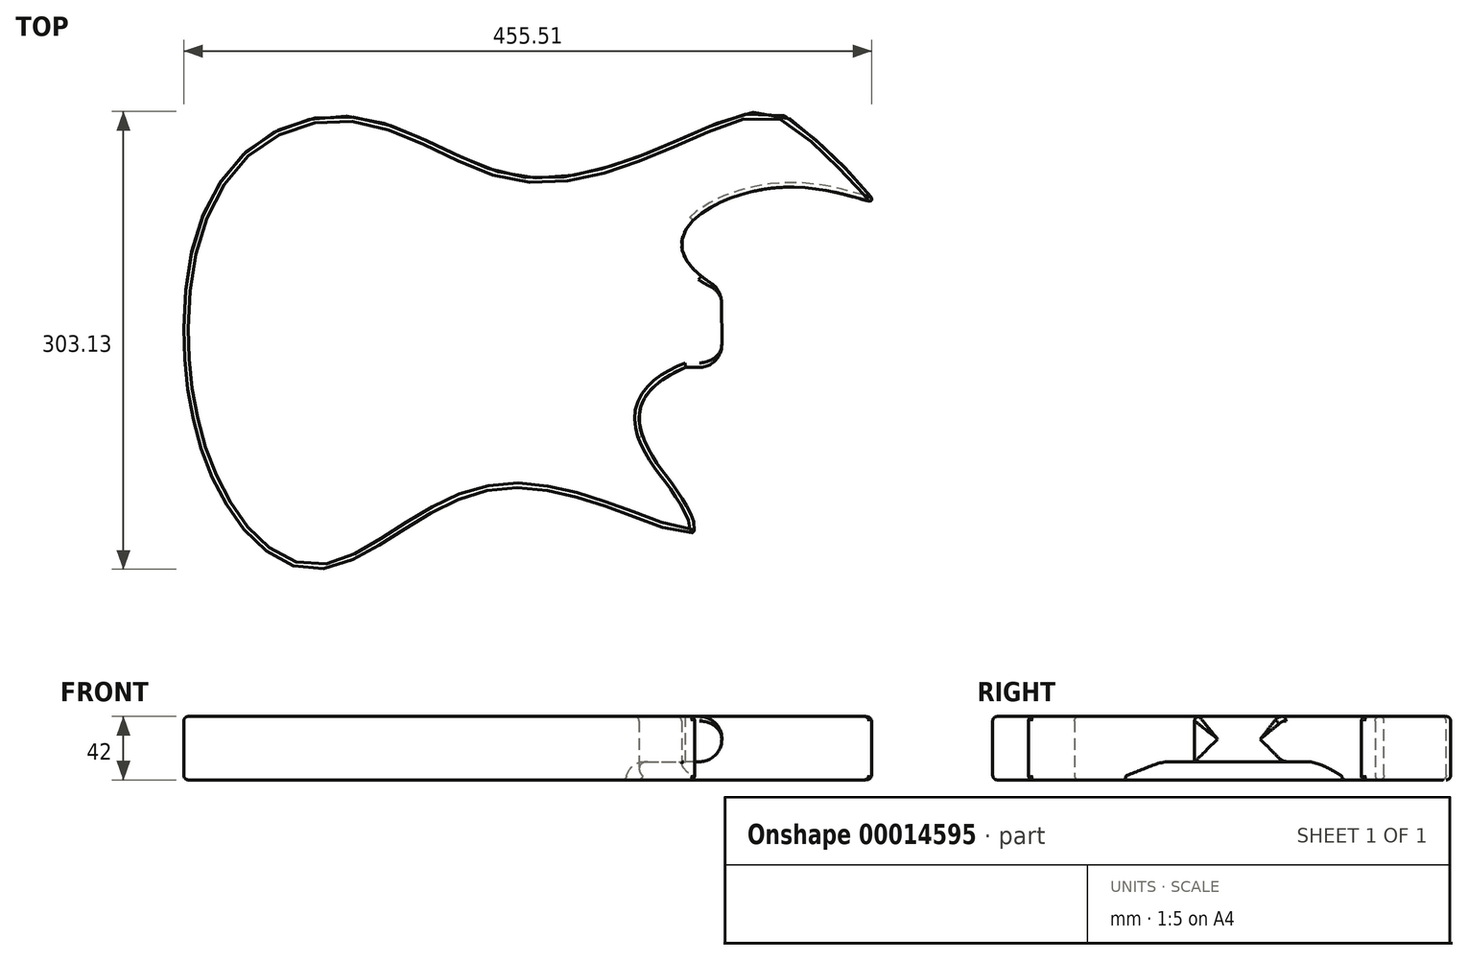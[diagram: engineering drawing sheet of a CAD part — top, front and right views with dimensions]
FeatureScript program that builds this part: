
annotation { "Feature Type Name" : "Feature", "Feature Type Description" : "" }
export const myFeature = defineFeature(function(context is Context, id is Id, definition is map)
    precondition{}
    {
        {
            var Q0;
            Q0=qCreatedBy(makeId("Top.planeOp"),FACE);
            var sketch = newSketch(context, id + "F0", { "sketchPlane" : qUnion([Q0])});
            skLineSegment(sketch, "E0", {"start": v(0, 450.63) * mm, "end": v(0, -420.06) * mm, "construction": true});
            skLineSegment(sketch, "E1", {"start": v(-1025.75, 0) * mm, "end": v(982.4, 0) * mm, "construction": true});
            skLineSegment(sketch, "E2", {"start": v(647.37, 21.5) * mm, "end": v(0, 27.92) * mm, "construction": true});
            skLineSegment(sketch, "E3.0.MirrorCS", {"start": v(647.37, -21.5) * mm, "end": v(0, -27.92) * mm, "construction": true});
            skLineSegment(sketch, "E4.0.MirrorCS", {"start": v(964.42, -135) * mm, "end": v(-680.01, -135) * mm, "construction": true});
            skPoint(sketch, "E5", {"position": v(192.37, -26) * mm});
            skPoint(sketch, "E6", {"position": v(215.87, 25.78) * mm});
            skFitSpline(sketch, "E7", {"points": [v(-139.95, 0) * mm, v(-52.8, -159.6) * mm, v(73.18, -105.7) * mm, v(197.21, -135) * mm, v(184.87, -105.05) * mm, v(169.29, -82.97) * mm, v(192.37, -26) * mm], "startDerivative": vector(-8.4, -1150.65) * mm, "endDerivative": vector(902.54, 365.45) * mm});
            skFitSpline(sketch, "E8", {"points": [v(215.87, 25.78) * mm, v(246.74, 92.46) * mm, v(315.54, 85.04) * mm, v(281.76, 121.56) * mm, v(245.96, 143.5) * mm, v(174.14, 118.99) * mm, v(75.44, 101.73) * mm, v(-31.82, 140.35) * mm, v(-139.95, 0) * mm], "startDerivative": vector(-1467.14, 819.4) * mm, "endDerivative": vector(0, -1755.16) * mm});
            skLineSegment(sketch, "E9", {"start": v(215.87, 25.78) * mm, "end": v(216.38, -25.77) * mm});
            skLineSegment(sketch, "E10", {"start": v(216.38, -25.77) * mm, "end": v(192.37, -26) * mm});
            skSolve(sketch);
        }
        {
            var Q0;
            Q0=makeQuery(id+"F0.imprint","IMPRINT",FACE,{"disambiguationData":[TD([[makeQuery(id+"F0.imprint","IMPRINT",EDGE,{"derivedFrom":sQuery(id+"F0.wireOp",EDGE,"E7")}),1.0]])]});
            extrude(context, id + "F1", {"entities" : qUnion([Q0]), "oppositeDirection" : true, "depth" : 42 * mm});
        }
        {
            var Q0;
            Q0=makeQuery(id+"F1.opExtrude","CAP_FACE",FACE,{"disambiguationData":[OSD([sQuery(id+"F0.wireOp",EDGE,"E7"),sQuery(id+"F0.wireOp",EDGE,"E8"),sQuery(id+"F0.wireOp",EDGE,"E9"),sQuery(id+"F0.wireOp",EDGE,"E10")])],"isStart":false});
            var sketch = newSketch(context, id + "F2", { "sketchPlane" : qUnion([Q0])});
            skArc(sketch, "E11", {"start": v(167.67, 80.11) * mm, "mid": v(155.83, -4.5) * mm, "end": v(202.55, -76.02) * mm});
            skLineSegment(sketch, "E12", {"start": v(202.55, -76.02) * mm, "end": v(243.56, 30.37) * mm});
            skLineSegment(sketch, "E13", {"start": v(243.56, 30.37) * mm, "end": v(167.67, 80.11) * mm});
            skSolve(sketch);
        }
        {
            var Q0;
            Q0 = qSketchRegion(id + "F2", true);
            extrude(context, id + "F3", {"entities" : qUnion([Q0]), "operationType" : NewBodyOperationType.REMOVE, "oppositeDirection" : true, "depth" : 12 * mm});
        }
        {
            var Q0;
            Q0=makeQuery(id+"F3.boolean.opBoolean","COPY",EDGE,{"derivedFrom":makeQuery(id+"F3.opExtrude","CAP_EDGE",EDGE,{"disambiguationData":[OSD([sQuery(id+"F2.wireOp",EDGE,"E11")])],"isStart":false})});
            fillet(context, id + "F4", {"entities" : qUnion([Q0]), "radius" : 12 * mm, "allowEdgeOverflow" : false});
        }
        {
            var Q0;
            Q0=makeQuery(id+"F1.opExtrude","CAP_FACE",FACE,{"disambiguationData":[OSD([sQuery(id+"F0.wireOp",EDGE,"E7"),sQuery(id+"F0.wireOp",EDGE,"E8"),sQuery(id+"F0.wireOp",EDGE,"E9"),sQuery(id+"F0.wireOp",EDGE,"E10")])],"isStart":false});
            fillet(context, id + "F5", {"entities" : qUnion([Q0]), "radius" : 3 * mm, "tangentPropagation" : true, "allowEdgeOverflow" : false});
        }
        {
            var Q0;
            Q0=makeQuery(id+"F1.opExtrude","CAP_EDGE",EDGE,{"disambiguationData":[OSD([sQuery(id+"F0.wireOp",EDGE,"E8")])],"isStart":true});
            var Q1;
            Q1=makeQuery(id+"F1.opExtrude","CAP_EDGE",EDGE,{"disambiguationData":[OSD([sQuery(id+"F0.wireOp",EDGE,"E7")])],"isStart":true});
            var Q2;
            Q2=makeQuery(id+"F1.opExtrude","CAP_EDGE",EDGE,{"disambiguationData":[OSD([sQuery(id+"F0.wireOp",EDGE,"E10")])],"isStart":true});
            fillet(context, id + "F6", {"entities" : qUnion([Q0, Q1, Q2]), "radius" : 3 * mm, "tangentPropagation" : true, "allowEdgeOverflow" : false});
        }
        {
            var Q0;
            Q0=makeQuery(id+"F1.opExtrude","SWEPT_FACE",FACE,{"disambiguationData":[OSD([sQuery(id+"F0.wireOp",EDGE,"E9")])]});
            fillet(context, id + "F7", {"entities" : qUnion([Q0]), "radius" : 15 * mm, "tangentPropagation" : true, "allowEdgeOverflow" : false});
        }
    });
